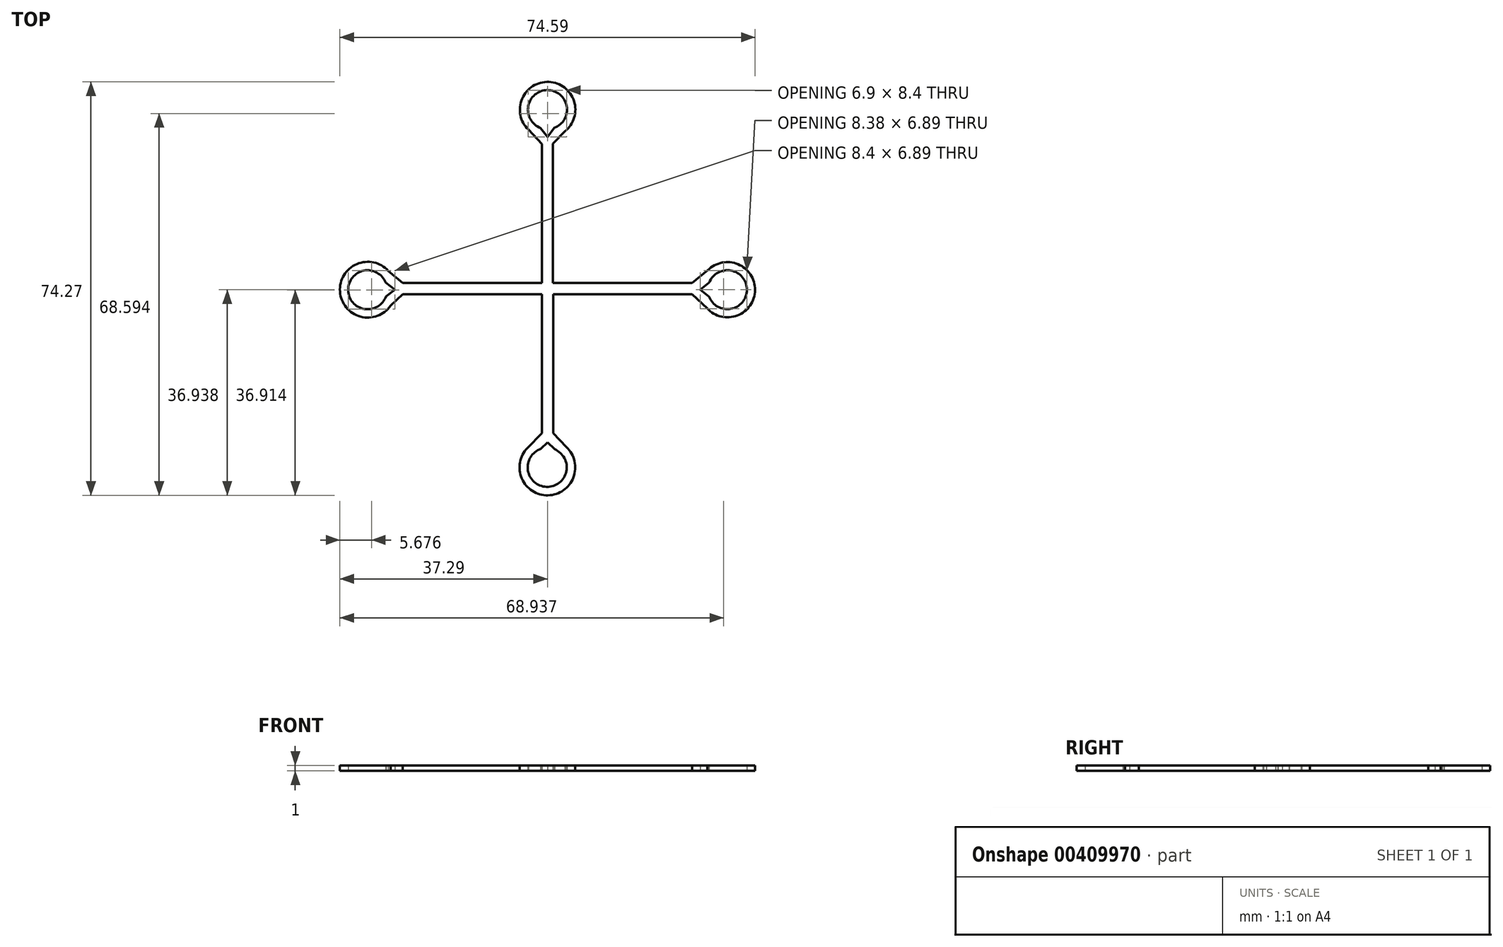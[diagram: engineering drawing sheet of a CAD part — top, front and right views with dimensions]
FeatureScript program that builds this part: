
annotation { "Feature Type Name" : "Feature", "Feature Type Description" : "" }
export const myFeature = defineFeature(function(context is Context, id is Id, definition is map)
    precondition{}
    {
        {
            var Q0;
            Q0=qCreatedBy(makeId("Top.planeOp"),FACE);
            var sketch = newSketch(context, id + "F0", { "sketchPlane" : qUnion([Q0])});
            skCircle(sketch, "E0", {"center": v(-32.32, -0.23) * mm, "radius": 3.5 * mm});
            skPoint(sketch, "E0.first.point", {"position": v(-34.96, 2.08) * mm});
            skPoint(sketch, "E0.second.point", {"position": v(-29.75, 2.14) * mm});
            skPoint(sketch, "E0.third.point", {"position": v(-31.43, -3.61) * mm});
            skCircle(sketch, "E1", {"center": v(-32.29, -0.21) * mm, "radius": 5.01 * mm});
            skPoint(sketch, "E1.first.point", {"position": v(-35.13, -4.34) * mm});
            skPoint(sketch, "E1.second.point", {"position": v(-28.33, 2.87) * mm});
            skPoint(sketch, "E1.third.point", {"position": v(-34.54, 4.26) * mm});
            skCircle(sketch, "E2", {"center": v(0, 32.13) * mm, "radius": 3.5 * mm});
            skPoint(sketch, "E2.first.point", {"position": v(0, 35.64) * mm});
            skPoint(sketch, "E2.second.point", {"position": v(3.48, 31.74) * mm});
            skPoint(sketch, "E2.third.point", {"position": v(-3.5, 31.73) * mm});
            skCircle(sketch, "E3", {"center": v(0.02, 32.13) * mm, "radius": 4.99 * mm});
            skPoint(sketch, "E3.first.point", {"position": v(0, 37.12) * mm});
            skPoint(sketch, "E3.second.point", {"position": v(5, 31.74) * mm});
            skPoint(sketch, "E3.third.point", {"position": v(-3.87, 29.01) * mm});
            skCircle(sketch, "E4", {"center": v(32.32, -0.2) * mm, "radius": 3.5 * mm});
            skPoint(sketch, "E4.first.point", {"position": v(35.3, 1.64) * mm});
            skPoint(sketch, "E4.second.point", {"position": v(29.83, -2.68) * mm});
            skPoint(sketch, "E4.third.point", {"position": v(35.32, -2.02) * mm});
            skCircle(sketch, "E5", {"center": v(32.33, -0.2) * mm, "radius": 4.96 * mm});
            skPoint(sketch, "E5.first.point", {"position": v(29.35, -4.18) * mm});
            skPoint(sketch, "E5.second.point", {"position": v(37.29, -0.2) * mm});
            skPoint(sketch, "E5.third.point", {"position": v(31.54, 4.69) * mm});
            skCircle(sketch, "E6", {"center": v(-0.05, -32.12) * mm, "radius": 3.5 * mm});
            skPoint(sketch, "E6.first.point", {"position": v(-2.2, -29.34) * mm});
            skPoint(sketch, "E6.second.point", {"position": v(2.74, -30) * mm});
            skPoint(sketch, "E6.third.point", {"position": v(0, -35.63) * mm});
            skCircle(sketch, "E7", {"center": v(-0.02, -32.14) * mm, "radius": 5 * mm});
            skPoint(sketch, "E7.first.point", {"position": v(-3.46, -35.78) * mm});
            skPoint(sketch, "E7.second.point", {"position": v(4, -29.16) * mm});
            skPoint(sketch, "E7.third.point", {"position": v(-3.03, -28.13) * mm});
            skPoint(sketch, "E8", {"position": v(0, -27.6) * mm});
            skPoint(sketch, "E9", {"position": v(-27.42, -0.2) * mm});
            skPoint(sketch, "E10", {"position": v(27.45, -0.2) * mm});
            skPoint(sketch, "E11", {"position": v(0, 27.25) * mm});
            skLineSegment(sketch, "E12", {"start": v(-29.06, 1.04) * mm, "end": v(-27.42, -0.2) * mm});
            skLineSegment(sketch, "E13", {"start": v(-29.03, -1.42) * mm, "end": v(-27.42, -0.2) * mm});
            skLineSegment(sketch, "E14", {"start": v(-1.17, -28.8) * mm, "end": v(0, -27.6) * mm});
            skLineSegment(sketch, "E15", {"start": v(0, -27.6) * mm, "end": v(1.25, -28.86) * mm});
            skLineSegment(sketch, "E16", {"start": v(29.04, -1.44) * mm, "end": v(27.45, -0.2) * mm});
            skLineSegment(sketch, "E17", {"start": v(29.05, 1.06) * mm, "end": v(27.45, -0.2) * mm});
            skLineSegment(sketch, "E18", {"start": v(-1.23, 28.85) * mm, "end": v(0, 27.25) * mm});
            skLineSegment(sketch, "E19", {"start": v(1.25, 28.86) * mm, "end": v(0, 27.25) * mm});
            skPoint(sketch, "E20", {"position": v(-1.02, 1.03) * mm});
            skPoint(sketch, "E21", {"position": v(-1.02, -1) * mm});
            skPoint(sketch, "E22", {"position": v(1.02, -1.01) * mm});
            skPoint(sketch, "E23", {"position": v(0.99, 1.03) * mm});
            skLineSegment(sketch, "E24", {"start": v(-1.02, 1.03) * mm, "end": v(-27.43, 1.03) * mm});
            skLineSegment(sketch, "E25", {"start": v(-1.02, -1) * mm, "end": v(-27.34, -1) * mm});
            skLineSegment(sketch, "E26", {"start": v(-26, -1) * mm, "end": v(-28.16, -3.05) * mm});
            skLineSegment(sketch, "E27", {"start": v(-1.02, 1.03) * mm, "end": v(-1.02, -1) * mm});
            skLineSegment(sketch, "E28", {"start": v(-1.02, 1.03) * mm, "end": v(0.99, 1.03) * mm});
            skLineSegment(sketch, "E29", {"start": v(0.99, 1.03) * mm, "end": v(1.02, -1.01) * mm});
            skLineSegment(sketch, "E30", {"start": v(1.02, -1.01) * mm, "end": v(-1.02, -1) * mm});
            skLineSegment(sketch, "E31", {"start": v(-1.02, 1.03) * mm, "end": v(-1.02, 26) * mm});
            skLineSegment(sketch, "E32", {"start": v(0.99, 1.03) * mm, "end": v(0.99, 26) * mm});
            skLineSegment(sketch, "E33", {"start": v(-1.02, 26) * mm, "end": v(-3.44, 28.53) * mm});
            skLineSegment(sketch, "E34", {"start": v(0.99, 26) * mm, "end": v(3.13, 28.23) * mm});
            skLineSegment(sketch, "E35", {"start": v(0.99, 1.03) * mm, "end": v(25.99, 1.03) * mm});
            skLineSegment(sketch, "E36", {"start": v(1.02, -1.01) * mm, "end": v(26, -1.01) * mm});
            skLineSegment(sketch, "E37", {"start": v(26, -1.01) * mm, "end": v(28.7, -3.59) * mm});
            skLineSegment(sketch, "E38", {"start": v(-1.02, -1) * mm, "end": v(-1.02, -26) * mm});
            skLineSegment(sketch, "E39", {"start": v(1.02, -1.01) * mm, "end": v(1.02, -25.98) * mm});
            skLineSegment(sketch, "E40", {"start": v(25.99, 1.03) * mm, "end": v(28.8, 3.28) * mm});
            skPoint(sketch, "E41", {"position": v(-26, 1.03) * mm});
            skLineSegment(sketch, "E42", {"start": v(-26, 1.03) * mm, "end": v(-28.6, 3.17) * mm});
            skLineSegment(sketch, "E43", {"start": v(-1.02, -26) * mm, "end": v(-3.6, -28.64) * mm});
            skLineSegment(sketch, "E44", {"start": v(1.02, -25.98) * mm, "end": v(3.79, -28.89) * mm});
            skSolve(sketch);
        }
        {
            var Q0;
            Q0 = qSketchRegion(id + "F0", true);
            extrude(context, id + "F1", {"entities" : qUnion([Q0]), "depth" : 1 * mm});
        }
    });
